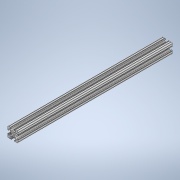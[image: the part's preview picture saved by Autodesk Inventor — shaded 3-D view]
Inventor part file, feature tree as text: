
AUTODESK INVENTOR PART (.ipt)
format: ipt  version: 2020 (Build 240168000, 168)  size: 236,032 bytes
history: native  units: in
note: dims shown in document units (in); Inventor stores cm internally (conversion verified against a paired STEP export)
features: extrude x1, sketch x1
ambient origin geometry x8: Origin, YZ Plane, XZ Plane, XY Plane, X Axis, Y Axis, Z Axis, Center Point
bodies: Solid1 (feature_tree)
feature tree (2):
  extrude  "Extrusion1"  [1 undecoded]
  sketch  "Sketch1"  dims[d0=15.0in d1=0.0in]
note: 1 required parameter value undecoded (feature->parameter linkage not recoverable at this tier; creation-order binding heuristic only, values carry confidence <= 0.55)
